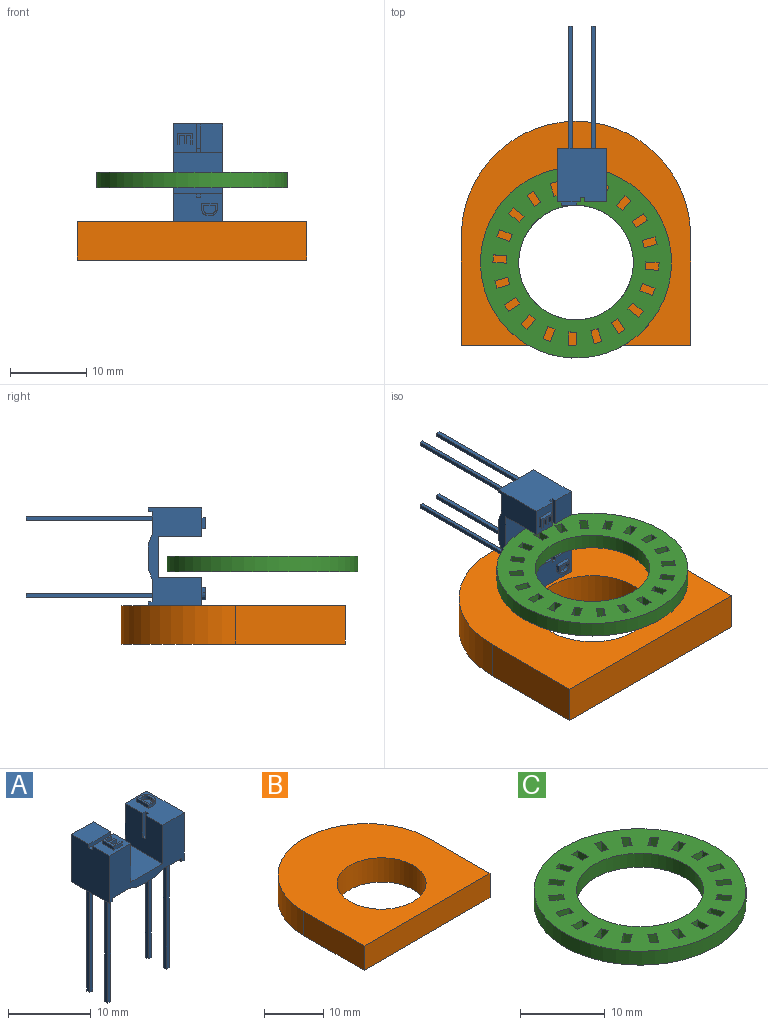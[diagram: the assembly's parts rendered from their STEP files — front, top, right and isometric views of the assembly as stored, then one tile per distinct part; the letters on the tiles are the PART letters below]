
ASSEMBLY  parts=3 mates=2
PART A: 81 faces, bbox 12.8x6.4x23.5 mm
  f0: plane 6.4x0.5mm, normal (0,0,-1), area 3.2mm2, adj f5,f6,f8,f58
  f1: plane 6.4x3.4mm, normal (0,0,-1), area 21.8mm2, adj f6,f8,f55,f60
  f2: plane 6.4x3.7mm, normal (0,0,1), area 20.4mm2, adj f6,f7,f8,f12,f13,f14,f15,f27
  f3: plane 3.7x2.93mm, normal (0,0,1), area 9.5mm2, adj f5,f6,f10,f18,f42,f43,f44,f45
  f4: plane 6.4x5.4mm, normal (0,0,1), area 34.6mm2, adj f6,f8,f10,f12
  f5: plane 7x6.4mm, normal (-1,0,0), area 44.5mm2, adj f0,f3,f6,f8,f11,f18,f19,f21
  f6: plane 12.8x7mm, normal (0,-1,0), area 55.2mm2, adj f0,f1,f2,f3,f4,f5,f7,f9
  f7: plane 7x6.4mm, normal (1,0,0), area 44.8mm2, adj f2,f6,f8,f9
  f8: plane 12.8x7mm, normal (0,1,0), area 55.2mm2, adj f0,f1,f2,f4,f5,f7,f9,f10
  f9: plane 6.4x0.5mm, normal (0,0,-1), area 3.2mm2, adj f6,f7,f8,f57
  f10: plane 6.4x5.7mm, normal (1,0,0), area 34.6mm2, adj f3,f4,f6,f8,f11,f17,f18,f19
  f11: plane 3.7x2.93mm, normal (0,0,1), area 10.8mm2, adj f5,f8,f10,f19
  f12: plane 6.4x5.7mm, normal (-1,0,0), area 34.6mm2, adj f2,f4,f6,f8,f13,f14,f16
  f13: plane 3.5x0.5mm, normal (0,-1,0), area 1.8mm2, adj f2,f12,f15,f16
  f14: plane 3.5x0.5mm, normal (0,1,0), area 1.8mm2, adj f2,f12,f15,f16
  f15: plane 3.5x0.55mm, normal (-1,0,0), area 1.8mm2, adj f2,f13,f14,f16,f22
  f16: plane 0.55x0.5mm, normal (0,0,1), area 0.3mm2, adj f12,f13,f14,f15
  f17: plane 0.55x0.5mm, normal (0,0,1), area 0.3mm2, adj f10,f18,f19,f20
  f18: plane 3.7x3.5mm, normal (0,1,0), area 3.5mm2, adj f3,f5,f10,f17,f20,f21
  f19: plane 3.7x3.5mm, normal (0,-1,0), area 3.5mm2, adj f5,f10,f11,f17,f20,f21
  f20: plane 2.95x0.55mm, normal (1,0,0), area 1.5mm2, adj f17,f18,f19,f21,f24
  f21: plane 3.2x0.55mm, normal (0,0,1), area 1.8mm2, adj f5,f18,f19,f20
  f22: cylinder r=0.2mm len=0.5mm, axis (-1,0,0), area 0.6mm2, adj f15,f23
  f23: plane 0.4x0.4mm, normal (-1,0,0), area 0.1mm2, adj f22
  f24: cylinder r=0.2mm len=0.4mm, axis (-1,0,0), area 0.1mm2, adj f20,f25
  f25: plane 0.4x0.4mm, normal (1,0,0), area 0.1mm2, adj f24
  f26: plane 2x1.64mm, normal (0,0,1), area 1.5mm2, adj f27,f28,f29,f30,f31,f32,f33,f34
  f27: plane 0.72x0.5mm, normal (0,-1,0), area 0.4mm2, adj f2,f26,f28,f33
  f28: extruded ~1.01x0.92mm, area 0.8mm2, adj f2,f26,f27,f29
  f29: extruded ~0.82x0.5mm, area 0.5mm2, adj f2,f26,f28,f30
  f30: cylinder r=0.67mm len=0.5mm, axis (0,0,-1), area 0.2mm2, adj f2,f26,f29,f31
  f31: extruded ~0.5x0.35mm, area 0.2mm2, adj f2,f26,f30,f32
  f32: plane 0.68x0.5mm, normal (0,1,0), area 0.3mm2, adj f2,f26,f31,f33
  f33: plane 2x0.5mm, normal (-1,0,0), area 1mm2, adj f2,f26,f27,f32
  f34: plane 1.54x0.5mm, normal (1,0,0), area 0.8mm2, adj f26,f35,f40,f41
  f35: plane 0.5x0.41mm, normal (0,1,0), area 0.2mm2, adj f26,f34,f36,f41
  f36: extruded ~0.5x0.47mm, area 0.3mm2, adj f26,f35,f37,f41
  f37: extruded ~0.64x0.5mm, area 0.3mm2, adj f26,f36,f38,f41
  f38: extruded ~0.71x0.5mm, area 0.4mm2, adj f26,f37,f39,f41
  f39: extruded ~0.5x0.33mm, area 0.2mm2, adj f26,f38,f40,f41
  f40: plane 0.5x0.41mm, normal (0,-1,0), area 0.2mm2, adj f26,f34,f39,f41
  f41: plane 1.54x1.08mm, normal (0,0,1), area 1.5mm2, adj f34,f35,f36,f37,f38,f39,f40
  f42: plane 1.46x0.5mm, normal (0,-1,0), area 0.7mm2, adj f3,f43,f53,f54
  f43: plane 0.5x0.23mm, normal (1,0,0), area 0.1mm2, adj f3,f42,f44,f54
  f44: plane 1.18x0.5mm, normal (0,1,0), area 0.6mm2, adj f3,f43,f45,f54
  f45: plane 0.69x0.5mm, normal (1,0,0), area 0.3mm2, adj f3,f44,f46,f54
  f46: plane 1.05x0.5mm, normal (0,-1,0), area 0.5mm2, adj f3,f45,f47,f54
  f47: plane 0.5x0.23mm, normal (1,0,0), area 0.1mm2, adj f3,f46,f48,f54
  f48: plane 1.05x0.5mm, normal (0,1,0), area 0.5mm2, adj f3,f47,f49,f54
  f49: plane 0.62x0.5mm, normal (1,0,0), area 0.3mm2, adj f3,f48,f50,f54
  f50: plane 1.13x0.5mm, normal (0,-1,0), area 0.6mm2, adj f3,f49,f51,f54
  f51: plane 0.5x0.23mm, normal (1,0,0), area 0.1mm2, adj f3,f50,f52,f54
  f52: plane 1.41x0.5mm, normal (0,1,0), area 0.7mm2, adj f3,f51,f53,f54
  f53: plane 2x0.5mm, normal (-1,0,0), area 1mm2, adj f3,f42,f52,f54
  f54: plane 2x1.46mm, normal (0,0,1), area 1.3mm2, adj f42,f43,f44,f45,f46,f47,f48,f49
  f55: plane 6.4x1.2mm, normal (0.38,0,-0.92), area 8.3mm2, adj f1,f6,f8,f56
  f56: plane 6.4x3mm, normal (0,0,-1), area 18.7mm2, adj f6,f8,f55,f57,f71,f72,f73,f74
  f57: plane 6.4x0.5mm, normal (-1,0,0), area 3.2mm2, adj f6,f8,f9,f56
  f58: plane 6.4x0.5mm, normal (1,0,0), area 3.2mm2, adj f0,f6,f8,f59
  f59: plane 6.4x3mm, normal (0,0,-1), area 18.7mm2, adj f6,f8,f58,f60,f61,f62,f63,f64
  f60: plane 6.4x1.2mm, normal (-0.38,0,-0.92), area 8.3mm2, adj f1,f6,f8,f59
  f61: plane 16.5x0.5mm, normal (-1,0,0), area 8.2mm2, adj f59,f62,f64,f65
  f62: plane 16.5x0.5mm, normal (0,-1,0), area 8.3mm2, adj f59,f61,f63,f65
  f63: plane 16.5x0.5mm, normal (1,0,0), area 8.2mm2, adj f59,f62,f64,f65
  f64: plane 16.5x0.5mm, normal (0,1,0), area 8.3mm2, adj f59,f61,f63,f65
  f65: plane 0.5x0.5mm, normal (0,0,-1), area 0.3mm2, adj f61,f62,f63,f64
  f66: plane 16.5x0.5mm, normal (-1,0,0), area 8.2mm2, adj f59,f67,f69,f70
  f67: plane 16.5x0.5mm, normal (0,-1,0), area 8.3mm2, adj f59,f66,f68,f70
  f68: plane 16.5x0.5mm, normal (1,0,0), area 8.2mm2, adj f59,f67,f69,f70
  f69: plane 16.5x0.5mm, normal (0,1,0), area 8.3mm2, adj f59,f66,f68,f70
  f70: plane 0.5x0.5mm, normal (0,0,-1), area 0.3mm2, adj f66,f67,f68,f69
  f71: plane 16.5x0.5mm, normal (-1,0,0), area 8.2mm2, adj f56,f72,f74,f75
  f72: plane 16.5x0.5mm, normal (0,-1,0), area 8.3mm2, adj f56,f71,f73,f75
  f73: plane 16.5x0.5mm, normal (1,0,0), area 8.2mm2, adj f56,f72,f74,f75
  f74: plane 16.5x0.5mm, normal (0,1,0), area 8.3mm2, adj f56,f71,f73,f75
  f75: plane 0.5x0.5mm, normal (0,0,-1), area 0.3mm2, adj f71,f72,f73,f74
  f76: plane 16.5x0.5mm, normal (-1,0,0), area 8.2mm2, adj f56,f77,f79,f80
  f77: plane 16.5x0.5mm, normal (0,-1,0), area 8.3mm2, adj f56,f76,f78,f80
  f78: plane 16.5x0.5mm, normal (1,0,0), area 8.2mm2, adj f56,f77,f79,f80
  f79: plane 16.5x0.5mm, normal (0,1,0), area 8.3mm2, adj f56,f76,f78,f80
  f80: plane 0.5x0.5mm, normal (0,0,-1), area 0.3mm2, adj f76,f77,f78,f79
PART B: 7 faces, bbox 30x29.3x5 mm
  f0: plane 14.33x5mm, normal (-1,0,0), area 71.6mm2, adj f1,f4,f5,f6
  f1: plane 30x5mm, normal (0,-1,0), area 150mm2, adj f0,f2,f5,f6
  f2: plane 14.33x5mm, normal (1,0,0), area 71.6mm2, adj f1,f4,f5,f6
  f3: cylinder r=7.5mm len=15mm, axis (0,0,-1), area 235.6mm2, adj f5,f6
  f4: cylinder r=15mm len=30mm, axis (0,0,-1), area 235.6mm2, adj f0,f2,f5,f6
  f5: plane 30x29.33mm, normal (0,0,1), area 606.6mm2, adj f0,f1,f2,f3,f4
  f6: plane 30x29.33mm, normal (0,0,-1), area 606.6mm2, adj f0,f1,f2,f3,f4
PART C: 84 faces, bbox 25x25x2 mm
  f0: plane 2x1.66mm, normal (-0.95,-0.31,0), area 3.5mm2, adj f1,f81,f82,f83
  f1: plane 2x0.95mm, normal (-0.31,0.95,0), area 2mm2, adj f0,f2,f82,f83
  f2: plane 2x1.66mm, normal (0.95,0.31,0), area 3.5mm2, adj f1,f81,f82,f83
  f3: plane 2x1.42mm, normal (-0.81,-0.59,0), area 3.5mm2, adj f4,f60,f82,f83
  f4: plane 2x0.81mm, normal (-0.59,0.81,0), area 2mm2, adj f3,f5,f82,f83
  f5: plane 2x1.42mm, normal (0.81,0.59,0), area 3.5mm2, adj f4,f60,f82,f83
  f6: plane 2x1.42mm, normal (-0.59,-0.81,0), area 3.5mm2, adj f7,f61,f82,f83
  f7: plane 2x0.81mm, normal (-0.81,0.59,0), area 2mm2, adj f6,f8,f82,f83
  f8: plane 2x1.42mm, normal (0.59,0.81,0), area 3.5mm2, adj f7,f61,f82,f83
  f9: plane 2x1.66mm, normal (-0.31,-0.95,0), area 3.5mm2, adj f10,f62,f82,f83
  f10: plane 2x0.95mm, normal (-0.95,0.31,0), area 2mm2, adj f9,f11,f82,f83
  f11: plane 2x1.66mm, normal (0.31,0.95,0), area 3.5mm2, adj f10,f62,f82,f83
  f12: plane 2x1.75mm, normal (0,-1,0), area 3.5mm2, adj f13,f63,f82,f83
  f13: plane 2x1mm, normal (-1,0,0), area 2mm2, adj f12,f14,f82,f83
  f14: plane 2x1.75mm, normal (0,1,0), area 3.5mm2, adj f13,f63,f82,f83
  f15: plane 2x1.66mm, normal (0.31,-0.95,0), area 3.5mm2, adj f16,f64,f82,f83
  f16: plane 2x0.95mm, normal (-0.95,-0.31,0), area 2mm2, adj f15,f17,f82,f83
  f17: plane 2x1.66mm, normal (-0.31,0.95,0), area 3.5mm2, adj f16,f64,f82,f83
  f18: plane 2x1.42mm, normal (0.59,-0.81,0), area 3.5mm2, adj f19,f65,f82,f83
  f19: plane 2x0.81mm, normal (-0.81,-0.59,0), area 2mm2, adj f18,f20,f82,f83
  f20: plane 2x1.42mm, normal (-0.59,0.81,0), area 3.5mm2, adj f19,f65,f82,f83
  f21: plane 2x1.42mm, normal (0.81,-0.59,0), area 3.5mm2, adj f22,f66,f82,f83
  f22: plane 2x0.81mm, normal (-0.59,-0.81,0), area 2mm2, adj f21,f23,f82,f83
  f23: plane 2x1.42mm, normal (-0.81,0.59,0), area 3.5mm2, adj f22,f66,f82,f83
  f24: plane 2x1.66mm, normal (0.95,-0.31,0), area 3.5mm2, adj f25,f67,f82,f83
  f25: plane 2x0.95mm, normal (-0.31,-0.95,0), area 2mm2, adj f24,f26,f82,f83
  f26: plane 2x1.66mm, normal (-0.95,0.31,0), area 3.5mm2, adj f25,f67,f82,f83
  f27: plane 2x1.75mm, normal (1,0,0), area 3.5mm2, adj f28,f68,f82,f83
  f28: plane 2x1mm, normal (0,-1,0), area 2mm2, adj f27,f29,f82,f83
  f29: plane 2x1.75mm, normal (-1,0,0), area 3.5mm2, adj f28,f68,f82,f83
  f30: plane 2x1.66mm, normal (0.95,0.31,0), area 3.5mm2, adj f31,f69,f82,f83
  f31: plane 2x0.95mm, normal (0.31,-0.95,0), area 2mm2, adj f30,f32,f82,f83
  f32: plane 2x1.66mm, normal (-0.95,-0.31,0), area 3.5mm2, adj f31,f69,f82,f83
  f33: plane 2x1.42mm, normal (0.81,0.59,0), area 3.5mm2, adj f34,f70,f82,f83
  f34: plane 2x0.81mm, normal (0.59,-0.81,0), area 2mm2, adj f33,f35,f82,f83
  f35: plane 2x1.42mm, normal (-0.81,-0.59,0), area 3.5mm2, adj f34,f70,f82,f83
  f36: plane 2x1.42mm, normal (0.59,0.81,0), area 3.5mm2, adj f37,f71,f82,f83
  f37: plane 2x0.81mm, normal (0.81,-0.59,0), area 2mm2, adj f36,f38,f82,f83
  f38: plane 2x1.42mm, normal (-0.59,-0.81,0), area 3.5mm2, adj f37,f71,f82,f83
  f39: plane 2x1.66mm, normal (0.31,0.95,0), area 3.5mm2, adj f40,f72,f82,f83
  f40: plane 2x0.95mm, normal (0.95,-0.31,0), area 2mm2, adj f39,f41,f82,f83
  f41: plane 2x1.66mm, normal (-0.31,-0.95,0), area 3.5mm2, adj f40,f72,f82,f83
  f42: plane 2x1.75mm, normal (0,1,0), area 3.5mm2, adj f43,f73,f82,f83
  f43: plane 2x1mm, normal (1,0,0), area 2mm2, adj f42,f44,f82,f83
  f44: plane 2x1.75mm, normal (0,-1,0), area 3.5mm2, adj f43,f73,f82,f83
  f45: plane 2x1.66mm, normal (-0.31,0.95,0), area 3.5mm2, adj f46,f74,f82,f83
  f46: plane 2x0.95mm, normal (0.95,0.31,0), area 2mm2, adj f45,f47,f82,f83
  f47: plane 2x1.66mm, normal (0.31,-0.95,0), area 3.5mm2, adj f46,f74,f82,f83
  f48: plane 2x1.42mm, normal (-0.59,0.81,0), area 3.5mm2, adj f49,f75,f82,f83
  f49: plane 2x0.81mm, normal (0.81,0.59,0), area 2mm2, adj f48,f50,f82,f83
  f50: plane 2x1.42mm, normal (0.59,-0.81,0), area 3.5mm2, adj f49,f75,f82,f83
  f51: plane 2x1.42mm, normal (-0.81,0.59,0), area 3.5mm2, adj f52,f76,f82,f83
  f52: plane 2x0.81mm, normal (0.59,0.81,0), area 2mm2, adj f51,f53,f82,f83
  f53: plane 2x1.42mm, normal (0.81,-0.59,0), area 3.5mm2, adj f52,f76,f82,f83
  f54: plane 2x1.66mm, normal (-0.95,0.31,0), area 3.5mm2, adj f55,f77,f82,f83
  f55: plane 2x0.95mm, normal (0.31,0.95,0), area 2mm2, adj f54,f56,f82,f83
  f56: plane 2x1.66mm, normal (0.95,-0.31,0), area 3.5mm2, adj f55,f77,f82,f83
  f57: plane 2x1.75mm, normal (1,0,0), area 3.5mm2, adj f58,f80,f82,f83
  f58: plane 2x1mm, normal (0,-1,0), area 2mm2, adj f57,f59,f82,f83
  f59: plane 2x1.75mm, normal (-1,0,0), area 3.5mm2, adj f58,f80,f82,f83
  f60: plane 2x0.81mm, normal (0.59,-0.81,0), area 2mm2, adj f3,f5,f82,f83
  f61: plane 2x0.81mm, normal (0.81,-0.59,0), area 2mm2, adj f6,f8,f82,f83
  f62: plane 2x0.95mm, normal (0.95,-0.31,0), area 2mm2, adj f9,f11,f82,f83
  f63: plane 2x1mm, normal (1,0,0), area 2mm2, adj f12,f14,f82,f83
  f64: plane 2x0.95mm, normal (0.95,0.31,0), area 2mm2, adj f15,f17,f82,f83
  f65: plane 2x0.81mm, normal (0.81,0.59,0), area 2mm2, adj f18,f20,f82,f83
  f66: plane 2x0.81mm, normal (0.59,0.81,0), area 2mm2, adj f21,f23,f82,f83
  f67: plane 2x0.95mm, normal (0.31,0.95,0), area 2mm2, adj f24,f26,f82,f83
  f68: plane 2x1mm, normal (0,1,0), area 2mm2, adj f27,f29,f82,f83
  f69: plane 2x0.95mm, normal (-0.31,0.95,0), area 2mm2, adj f30,f32,f82,f83
  f70: plane 2x0.81mm, normal (-0.59,0.81,0), area 2mm2, adj f33,f35,f82,f83
  f71: plane 2x0.81mm, normal (-0.81,0.59,0), area 2mm2, adj f36,f38,f82,f83
  f72: plane 2x0.95mm, normal (-0.95,0.31,0), area 2mm2, adj f39,f41,f82,f83
  f73: plane 2x1mm, normal (-1,0,0), area 2mm2, adj f42,f44,f82,f83
  f74: plane 2x0.95mm, normal (-0.95,-0.31,0), area 2mm2, adj f45,f47,f82,f83
  f75: plane 2x0.81mm, normal (-0.81,-0.59,0), area 2mm2, adj f48,f50,f82,f83
  f76: plane 2x0.81mm, normal (-0.59,-0.81,0), area 2mm2, adj f51,f53,f82,f83
  f77: plane 2x0.95mm, normal (-0.31,-0.95,0), area 2mm2, adj f54,f56,f82,f83
  f78: cylinder r=12.5mm len=25mm, axis (0,0,-1), area 157.1mm2, adj f82,f83
  f79: cylinder r=7.5mm len=15mm, axis (0,0,-1), area 94.2mm2, adj f82,f83
  f80: plane 2x1mm, normal (0,1,0), area 2mm2, adj f57,f59,f82,f83
  f81: plane 2x0.95mm, normal (0.31,-0.95,0), area 2mm2, adj f0,f2,f82,f83
  f82: plane 25x25mm, normal (0,0,1), area 279.2mm2, adj f0,f1,f2,f3,f4,f5,f6,f7
  f83: plane 25x25mm, normal (0,0,-1), area 279.2mm2, adj f0,f1,f2,f3,f4,f5,f6,f7
PLACE A rot(axis=(0.58,0.58,-0.58),120deg) t=(0.96,11.19,8.9)mm
PLACE B t=(0.14,-3.76,-2.5)mm fixed
PLACE C rot(axis=(0,0,-1),92.7deg) t=(0.14,-3.76,6.97)mm
MATE planar A.f7 <-> B.f5  axis (0,0,-1) through (0.96,7.69,2.5)mm
MATE cylindrical C.f79 <-> B.f3  axis (0,0,1) through (0.14,-3.76,8.97)mm
